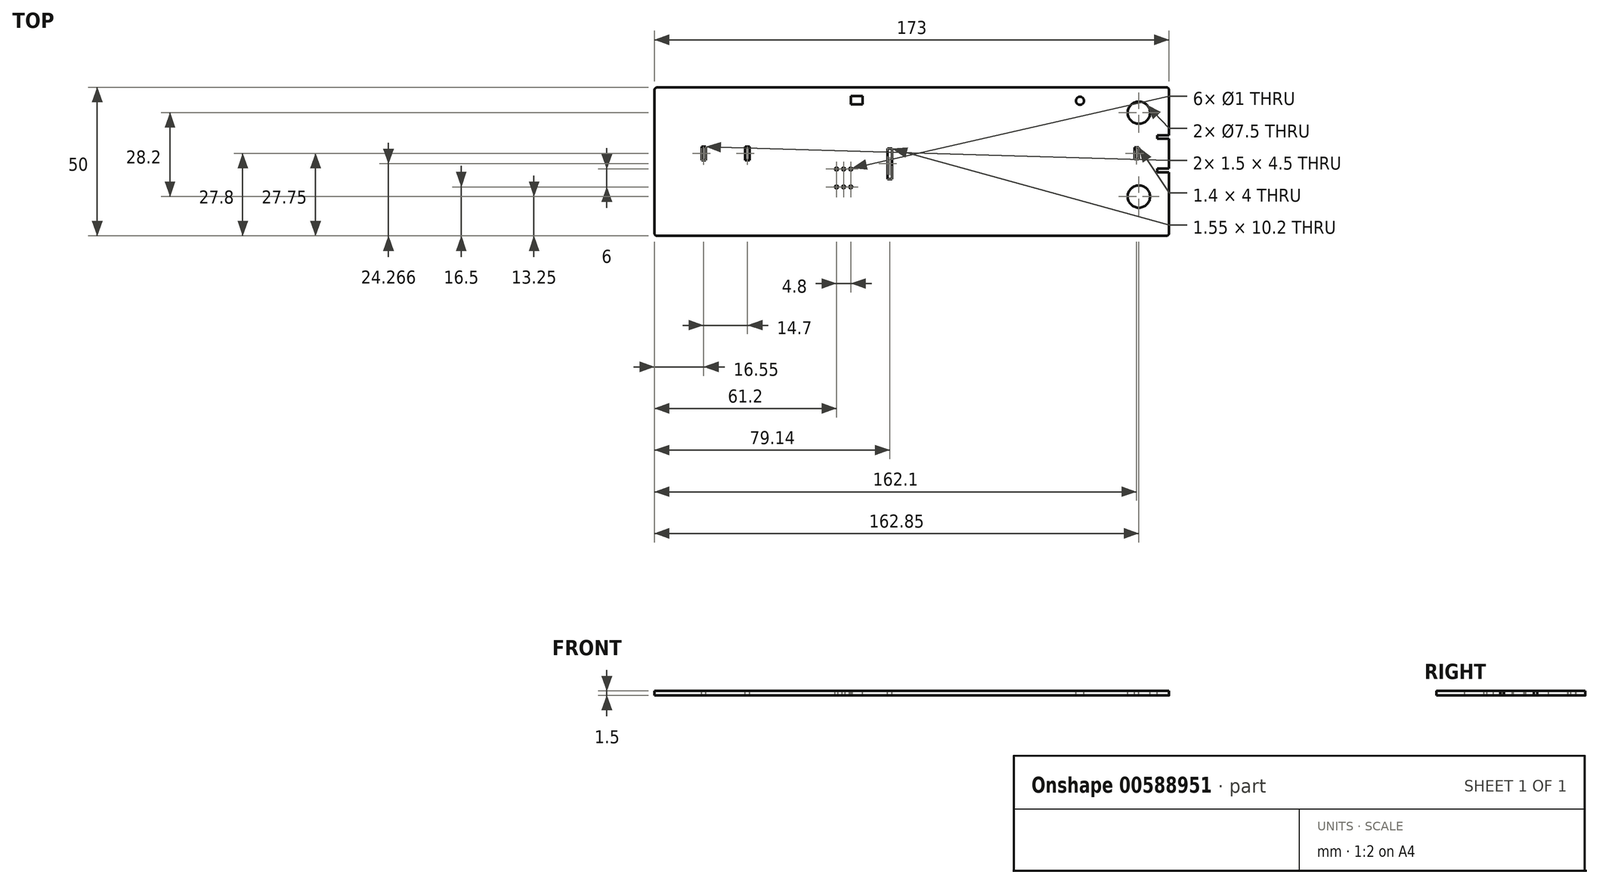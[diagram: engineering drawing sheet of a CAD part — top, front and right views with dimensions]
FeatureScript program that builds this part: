
annotation { "Feature Type Name" : "Feature", "Feature Type Description" : "" }
export const myFeature = defineFeature(function(context is Context, id is Id, definition is map)
    precondition{}
    {
        {
            var Q0;
            Q0=qCreatedBy(makeId("Top.planeOp"),FACE);
            var sketch = newSketch(context, id + "F0", { "sketchPlane" : qUnion([Q0])});
            skLineSegment(sketch, "E0.bottom", {"start": v(86.5, -25) * mm, "end": v(-86.5, -25) * mm});
            skLineSegment(sketch, "E0.top", {"start": v(86.5, 25) * mm, "end": v(-86.5, 25) * mm});
            skLineSegment(sketch, "E0.left", {"start": v(86.5, -25) * mm, "end": v(86.5, 25) * mm});
            skLineSegment(sketch, "E0.right", {"start": v(-86.5, -25) * mm, "end": v(-86.5, 25) * mm});
            skPoint(sketch, "E0.middle", {"position": v(0, 0) * mm});
            skSolve(sketch);
        }
        {
            var Q0;
            Q0=makeQuery(id+"F0.imprint","IMPRINT",FACE,{"disambiguationData":[TD([[makeQuery(id+"F0.imprint","IMPRINT",EDGE,{"derivedFrom":sQuery(id+"F0.wireOp",EDGE,"E0.bottom")}),-1.0]])]});
            extrude(context, id + "F1", {"entities" : qUnion([Q0]), "depth" : 1.5 * mm, "offsetDistance" : 25 * mm});
        }
        {
            var Q0;
            Q0=makeQuery(id+"F1.opExtrude","CAP_FACE",FACE,{"disambiguationData":[OSD([sQuery(id+"F0.wireOp",EDGE,"E0.bottom"),sQuery(id+"F0.wireOp",EDGE,"E0.top"),sQuery(id+"F0.wireOp",EDGE,"E0.left"),sQuery(id+"F0.wireOp",EDGE,"E0.right")])],"isStart":false});
            var sketch = newSketch(context, id + "F2", { "sketchPlane" : qUnion([Q0])});
            skLineSegment(sketch, "E1.bottom", {"start": v(-70.7, 5) * mm, "end": v(-69.2, 5) * mm});
            skLineSegment(sketch, "E1.top", {"start": v(-70.7, 0.5) * mm, "end": v(-69.2, 0.5) * mm});
            skLineSegment(sketch, "E1.left", {"start": v(-70.7, 5) * mm, "end": v(-70.7, 0.5) * mm});
            skLineSegment(sketch, "E1.right", {"start": v(-69.2, 5) * mm, "end": v(-69.2, 0.5) * mm});
            skSolve(sketch);
        }
        {
            var Q0;
            Q0=makeQuery(id+"F2.imprint","IMPRINT",FACE,{"disambiguationData":[TD([[makeQuery(id+"F2.imprint","IMPRINT",EDGE,{"derivedFrom":sQuery(id+"F2.wireOp",EDGE,"E1.bottom")}),1.0]])]});
            var sketch = newSketch(context, id + "F3", { "sketchPlane" : qUnion([Q0])});
            skLineSegment(sketch, "E2.bottom", {"start": v(-56, 5) * mm, "end": v(-54.5, 5) * mm});
            skLineSegment(sketch, "E2.top", {"start": v(-56, 0.5) * mm, "end": v(-54.5, 0.5) * mm});
            skLineSegment(sketch, "E2.left", {"start": v(-56, 5) * mm, "end": v(-56, 0.5) * mm});
            skLineSegment(sketch, "E2.right", {"start": v(-54.5, 5) * mm, "end": v(-54.5, 0.5) * mm});
            skSolve(sketch);
        }
        {
            var Q0;
            Q0=makeQuery(id+"F2.imprint","IMPRINT",FACE,{"disambiguationData":[TD([[makeQuery(id+"F2.imprint","IMPRINT",EDGE,{"derivedFrom":sQuery(id+"F2.wireOp",EDGE,"E1.bottom")}),-1.0]])]});
            extrude(context, id + "F4", {"entities" : qUnion([Q0]), "operationType" : NewBodyOperationType.REMOVE, "endBound" : BoundingType.THROUGH_ALL, "oppositeDirection" : true, "depth" : 25 * mm, "offsetDistance" : 25 * mm});
        }
        {
            var Q0;
            Q0=makeQuery(id+"F3.imprint","IMPRINT",FACE,{"disambiguationData":[TD([[makeQuery(id+"F3.imprint","IMPRINT",EDGE,{"derivedFrom":sQuery(id+"F3.wireOp",EDGE,"E2.bottom")}),-1.0]])]});
            extrude(context, id + "F5", {"entities" : qUnion([Q0]), "operationType" : NewBodyOperationType.REMOVE, "endBound" : BoundingType.THROUGH_ALL, "oppositeDirection" : true, "depth" : 25 * mm, "offsetDistance" : 25 * mm});
        }
        {
            var Q0;
            Q0=makeQuery(id+"F1.opExtrude","CAP_FACE",FACE,{"disambiguationData":[OSD([sQuery(id+"F0.wireOp",EDGE,"E0.bottom"),sQuery(id+"F0.wireOp",EDGE,"E0.top"),sQuery(id+"F0.wireOp",EDGE,"E0.left"),sQuery(id+"F0.wireOp",EDGE,"E0.right")])],"isStart":false});
            var sketch = newSketch(context, id + "F6", { "sketchPlane" : qUnion([Q0])});
            skLineSegment(sketch, "E3.bottom", {"start": v(-20.5, 22) * mm, "end": v(-16.5, 22) * mm});
            skLineSegment(sketch, "E3.top", {"start": v(-20.5, 19.3) * mm, "end": v(-16.5, 19.3) * mm});
            skLineSegment(sketch, "E3.left", {"start": v(-20.5, 22) * mm, "end": v(-20.5, 19.3) * mm});
            skLineSegment(sketch, "E3.right", {"start": v(-16.5, 22) * mm, "end": v(-16.5, 19.3) * mm});
            skSolve(sketch);
        }
        {
            var Q0;
            Q0=makeQuery(id+"F6.imprint","IMPRINT",FACE,{"disambiguationData":[TD([[makeQuery(id+"F6.imprint","IMPRINT",EDGE,{"derivedFrom":sQuery(id+"F6.wireOp",EDGE,"E3.bottom")}),-1.0]])]});
            extrude(context, id + "F7", {"entities" : qUnion([Q0]), "operationType" : NewBodyOperationType.REMOVE, "endBound" : BoundingType.THROUGH_ALL, "oppositeDirection" : true, "depth" : 25 * mm, "offsetDistance" : 25 * mm});
        }
        {
            var Q0;
            Q0=makeQuery(id+"F1.opExtrude","CAP_FACE",FACE,{"disambiguationData":[OSD([sQuery(id+"F0.wireOp",EDGE,"E0.bottom"),sQuery(id+"F0.wireOp",EDGE,"E0.top"),sQuery(id+"F0.wireOp",EDGE,"E0.left"),sQuery(id+"F0.wireOp",EDGE,"E0.right")])],"isStart":false});
            var sketch = newSketch(context, id + "F8", { "sketchPlane" : qUnion([Q0])});
            skCircle(sketch, "E4", {"center": v(56.55, 20.45) * mm, "radius": 1.35 * mm});
            skSolve(sketch);
        }
        {
            var Q0;
            Q0=makeQuery(id+"F8.imprint","IMPRINT",FACE,{"disambiguationData":[TD([[makeQuery(id+"F8.imprint","IMPRINT",EDGE,{"derivedFrom":sQuery(id+"F8.wireOp",EDGE,"E4")}),1.0]])]});
            extrude(context, id + "F9", {"entities" : qUnion([Q0]), "operationType" : NewBodyOperationType.REMOVE, "endBound" : BoundingType.THROUGH_ALL, "oppositeDirection" : true, "depth" : 25 * mm, "offsetDistance" : 25 * mm});
        }
        {
            var Q0;
            Q0=makeQuery(id+"F1.opExtrude","CAP_FACE",FACE,{"disambiguationData":[OSD([sQuery(id+"F0.wireOp",EDGE,"E0.bottom"),sQuery(id+"F0.wireOp",EDGE,"E0.top"),sQuery(id+"F0.wireOp",EDGE,"E0.left"),sQuery(id+"F0.wireOp",EDGE,"E0.right")])],"isStart":false});
            var sketch = newSketch(context, id + "F10", { "sketchPlane" : qUnion([Q0])});
            skCircle(sketch, "E5", {"center": v(76.35, 16.45) * mm, "radius": 3.75 * mm});
            skCircle(sketch, "E6", {"center": v(76.35, -11.75) * mm, "radius": 3.75 * mm});
            skSolve(sketch);
        }
        {
            var Q0;
            Q0=makeQuery(id+"F10.imprint","IMPRINT",FACE,{"disambiguationData":[TD([[makeQuery(id+"F10.imprint","IMPRINT",EDGE,{"derivedFrom":sQuery(id+"F10.wireOp",EDGE,"E5")}),1.0]])]});
            var Q1;
            Q1=makeQuery(id+"F10.imprint","IMPRINT",FACE,{"disambiguationData":[TD([[makeQuery(id+"F10.imprint","IMPRINT",EDGE,{"derivedFrom":sQuery(id+"F10.wireOp",EDGE,"E6")}),1.0]])]});
            extrude(context, id + "F11", {"entities" : qUnion([Q0, Q1]), "operationType" : NewBodyOperationType.REMOVE, "endBound" : BoundingType.THROUGH_ALL, "oppositeDirection" : true, "depth" : 25 * mm, "offsetDistance" : 25 * mm});
        }
        {
            var Q0;
            Q0=makeQuery(id+"F1.opExtrude","CAP_FACE",FACE,{"disambiguationData":[OSD([sQuery(id+"F0.wireOp",EDGE,"E0.bottom"),sQuery(id+"F0.wireOp",EDGE,"E0.top"),sQuery(id+"F0.wireOp",EDGE,"E0.left"),sQuery(id+"F0.wireOp",EDGE,"E0.right")])],"isStart":false});
            var sketch = newSketch(context, id + "F12", { "sketchPlane" : qUnion([Q0])});
            skLineSegment(sketch, "E7.bottom", {"start": v(86.5, 8.86) * mm, "end": v(82.5, 8.86) * mm});
            skLineSegment(sketch, "E7.top", {"start": v(86.5, 7.66) * mm, "end": v(82.5, 7.66) * mm});
            skLineSegment(sketch, "E7.left", {"start": v(86.5, 8.86) * mm, "end": v(86.5, 7.66) * mm});
            skLineSegment(sketch, "E7.right", {"start": v(82.5, 8.86) * mm, "end": v(82.5, 7.66) * mm});
            skLineSegment(sketch, "E8.bottom", {"start": v(86.5, -2.34) * mm, "end": v(82.5, -2.34) * mm});
            skLineSegment(sketch, "E8.top", {"start": v(86.5, -3.54) * mm, "end": v(82.5, -3.54) * mm});
            skLineSegment(sketch, "E8.left", {"start": v(86.5, -2.34) * mm, "end": v(86.5, -3.54) * mm});
            skLineSegment(sketch, "E8.right", {"start": v(82.5, -2.34) * mm, "end": v(82.5, -3.54) * mm});
            skSolve(sketch);
        }
        {
            var Q0;
            Q0=makeQuery(id+"F12.imprint","IMPRINT",FACE,{"disambiguationData":[TD([[makeQuery(id+"F12.imprint","IMPRINT",EDGE,{"derivedFrom":sQuery(id+"F12.wireOp",EDGE,"E7.bottom")}),1.0]])]});
            var Q1;
            Q1=makeQuery(id+"F12.imprint","IMPRINT",FACE,{"disambiguationData":[TD([[makeQuery(id+"F12.imprint","IMPRINT",EDGE,{"derivedFrom":sQuery(id+"F12.wireOp",EDGE,"E8.bottom")}),1.0]])]});
            extrude(context, id + "F13", {"entities" : qUnion([Q0, Q1]), "operationType" : NewBodyOperationType.REMOVE, "endBound" : BoundingType.THROUGH_ALL, "oppositeDirection" : true, "depth" : 25 * mm, "offsetDistance" : 25 * mm});
        }
        {
            var Q0;
            Q0=makeQuery(id+"F1.opExtrude","CAP_FACE",FACE,{"disambiguationData":[OSD([sQuery(id+"F0.wireOp",EDGE,"E0.bottom"),sQuery(id+"F0.wireOp",EDGE,"E0.top"),sQuery(id+"F0.wireOp",EDGE,"E0.left"),sQuery(id+"F0.wireOp",EDGE,"E0.right")])],"isStart":false});
            var sketch = newSketch(context, id + "F14", { "sketchPlane" : qUnion([Q0])});
            skLineSegment(sketch, "E9.bottom", {"start": v(74.9, 4.8) * mm, "end": v(76.3, 4.8) * mm});
            skLineSegment(sketch, "E9.top", {"start": v(74.9, 0.8) * mm, "end": v(76.3, 0.8) * mm});
            skLineSegment(sketch, "E9.left", {"start": v(74.9, 4.8) * mm, "end": v(74.9, 0.8) * mm});
            skLineSegment(sketch, "E9.right", {"start": v(76.3, 4.8) * mm, "end": v(76.3, 0.8) * mm});
            skSolve(sketch);
        }
        {
            var Q0;
            Q0=makeQuery(id+"F14.imprint","IMPRINT",FACE,{"disambiguationData":[TD([[makeQuery(id+"F14.imprint","IMPRINT",EDGE,{"derivedFrom":sQuery(id+"F14.wireOp",EDGE,"E9.bottom")}),-1.0]])]});
            extrude(context, id + "F15", {"entities" : qUnion([Q0]), "operationType" : NewBodyOperationType.REMOVE, "endBound" : BoundingType.THROUGH_ALL, "oppositeDirection" : true, "depth" : 25 * mm, "offsetDistance" : 25 * mm});
        }
        {
            var Q0;
            Q0=makeQuery(id+"F1.opExtrude","SWEPT_EDGE",EDGE,{"disambiguationData":[OSD([sQuery(id+"F0.wireOp",EDGE,"E0.bottom"),sQuery(id+"F0.wireOp",EDGE,"E0.right")])]});
            var Q1;
            Q1=makeQuery(id+"F1.opExtrude","SWEPT_EDGE",EDGE,{"disambiguationData":[OSD([sQuery(id+"F0.wireOp",EDGE,"E0.top"),sQuery(id+"F0.wireOp",EDGE,"E0.right")])]});
            var Q2;
            Q2=makeQuery(id+"F1.opExtrude","SWEPT_EDGE",EDGE,{"disambiguationData":[OSD([sQuery(id+"F0.wireOp",EDGE,"E0.top"),sQuery(id+"F0.wireOp",EDGE,"E0.left")])]});
            var Q3;
            Q3=makeQuery(id+"F1.opExtrude","SWEPT_EDGE",EDGE,{"disambiguationData":[OSD([sQuery(id+"F0.wireOp",EDGE,"E0.bottom"),sQuery(id+"F0.wireOp",EDGE,"E0.left")])]});
            fillet(context, id + "F16", {"entities" : qUnion([Q0, Q1, Q2, Q3]), "radius" : 1 * mm, "tangentPropagation" : true, "allowEdgeOverflow" : false});
        }
        {
            var Q0;
            Q0=makeQuery(id+"F1.opExtrude","CAP_FACE",FACE,{"disambiguationData":[OSD([sQuery(id+"F0.wireOp",EDGE,"E0.bottom"),sQuery(id+"F0.wireOp",EDGE,"E0.top"),sQuery(id+"F0.wireOp",EDGE,"E0.left"),sQuery(id+"F0.wireOp",EDGE,"E0.right")])],"isStart":false});
            var sketch = newSketch(context, id + "F17", { "sketchPlane" : qUnion([Q0])});
            skCircle(sketch, "E10", {"center": v(-25.3, -2.5) * mm, "radius": 0.5 * mm});
            skCircle(sketch, "E11", {"center": v(-22.9, -2.5) * mm, "radius": 0.5 * mm});
            skCircle(sketch, "E12", {"center": v(-20.5, -2.5) * mm, "radius": 0.5 * mm});
            skCircle(sketch, "E13", {"center": v(-25.3, -8.5) * mm, "radius": 0.5 * mm});
            skCircle(sketch, "E14", {"center": v(-22.9, -8.5) * mm, "radius": 0.5 * mm});
            skCircle(sketch, "E15", {"center": v(-20.5, -8.5) * mm, "radius": 0.5 * mm});
            skSolve(sketch);
        }
        {
            var Q0;
            Q0=makeQuery(id+"F17.imprint","IMPRINT",FACE,{"disambiguationData":[TD([[makeQuery(id+"F17.imprint","IMPRINT",EDGE,{"derivedFrom":sQuery(id+"F17.wireOp",EDGE,"E10")}),1.0]])]});
            var Q1;
            Q1=makeQuery(id+"F17.imprint","IMPRINT",FACE,{"disambiguationData":[TD([[makeQuery(id+"F17.imprint","IMPRINT",EDGE,{"derivedFrom":sQuery(id+"F17.wireOp",EDGE,"E11")}),1.0]])]});
            var Q2;
            Q2=makeQuery(id+"F17.imprint","IMPRINT",FACE,{"disambiguationData":[TD([[makeQuery(id+"F17.imprint","IMPRINT",EDGE,{"derivedFrom":sQuery(id+"F17.wireOp",EDGE,"E12")}),1.0]])]});
            var Q3;
            Q3=makeQuery(id+"F17.imprint","IMPRINT",FACE,{"disambiguationData":[TD([[makeQuery(id+"F17.imprint","IMPRINT",EDGE,{"derivedFrom":sQuery(id+"F17.wireOp",EDGE,"E15")}),1.0]])]});
            var Q4;
            Q4=makeQuery(id+"F17.imprint","IMPRINT",FACE,{"disambiguationData":[TD([[makeQuery(id+"F17.imprint","IMPRINT",EDGE,{"derivedFrom":sQuery(id+"F17.wireOp",EDGE,"E14")}),1.0]])]});
            var Q5;
            Q5=makeQuery(id+"F17.imprint","IMPRINT",FACE,{"disambiguationData":[TD([[makeQuery(id+"F17.imprint","IMPRINT",EDGE,{"derivedFrom":sQuery(id+"F17.wireOp",EDGE,"E13")}),1.0]])]});
            extrude(context, id + "F18", {"entities" : qUnion([Q0, Q1, Q2, Q3, Q4, Q5]), "operationType" : NewBodyOperationType.REMOVE, "endBound" : BoundingType.THROUGH_ALL, "oppositeDirection" : true, "depth" : 25 * mm, "offsetDistance" : 25 * mm});
        }
        {
            var Q0;
            Q0=makeQuery(id+"F1.opExtrude","CAP_FACE",FACE,{"disambiguationData":[OSD([sQuery(id+"F0.wireOp",EDGE,"E0.bottom"),sQuery(id+"F0.wireOp",EDGE,"E0.top"),sQuery(id+"F0.wireOp",EDGE,"E0.left"),sQuery(id+"F0.wireOp",EDGE,"E0.right")])],"isStart":false});
            var sketch = newSketch(context, id + "F19", { "sketchPlane" : qUnion([Q0])});
            skLineSegment(sketch, "E16.bottom", {"start": v(-8.14, 4.37) * mm, "end": v(-6.58, 4.37) * mm});
            skLineSegment(sketch, "E16.top", {"start": v(-8.14, -5.83) * mm, "end": v(-6.58, -5.83) * mm});
            skLineSegment(sketch, "E16.left", {"start": v(-8.14, 4.37) * mm, "end": v(-8.14, -5.83) * mm});
            skLineSegment(sketch, "E16.right", {"start": v(-6.58, 4.37) * mm, "end": v(-6.58, -5.83) * mm});
            skSolve(sketch);
        }
        {
            var Q0;
            Q0=makeQuery(id+"F19.imprint","IMPRINT",FACE,{"disambiguationData":[TD([[makeQuery(id+"F19.imprint","IMPRINT",EDGE,{"derivedFrom":sQuery(id+"F19.wireOp",EDGE,"E16.bottom")}),-1.0]])]});
            extrude(context, id + "F20", {"entities" : qUnion([Q0]), "operationType" : NewBodyOperationType.REMOVE, "endBound" : BoundingType.THROUGH_ALL, "oppositeDirection" : true, "depth" : 25 * mm, "offsetDistance" : 25 * mm});
        }
    });
